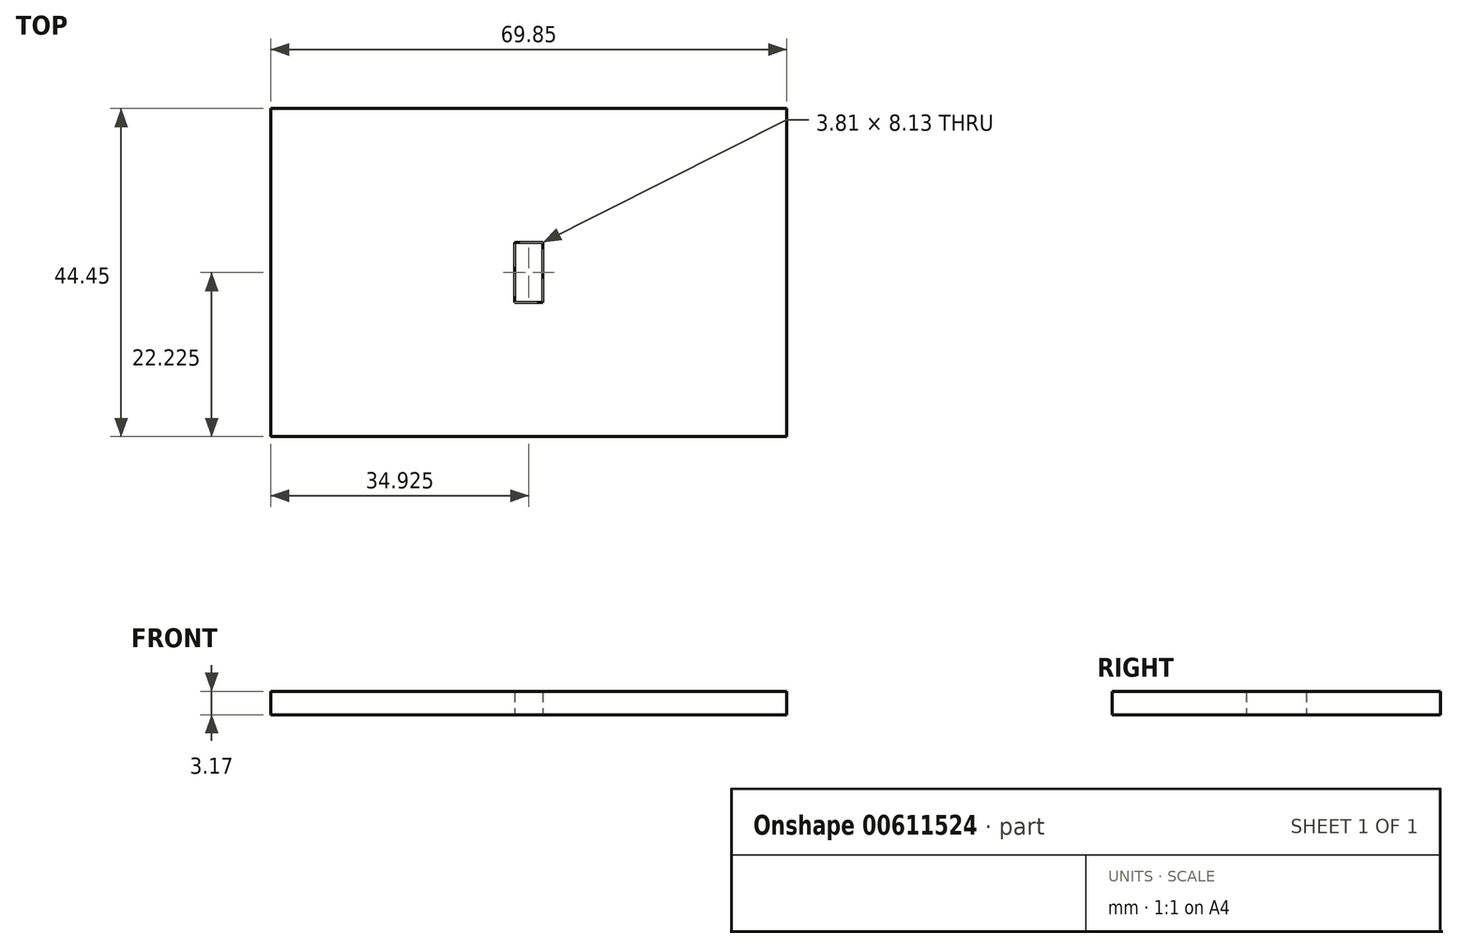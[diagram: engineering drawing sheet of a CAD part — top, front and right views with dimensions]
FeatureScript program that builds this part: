
annotation { "Feature Type Name" : "Feature", "Feature Type Description" : "" }
export const myFeature = defineFeature(function(context is Context, id is Id, definition is map)
    precondition{}
    {
        {
            var Q0;
            Q0=qCreatedBy(makeId("Top.planeOp"),FACE);
            var sketch = newSketch(context, id + "F0", { "sketchPlane" : qUnion([Q0])});
            skLineSegment(sketch, "E0.bottom", {"start": v(0, 0) * mm, "end": v(69.85, 0) * mm});
            skLineSegment(sketch, "E0.top", {"start": v(0, -44.45) * mm, "end": v(69.85, -44.45) * mm});
            skLineSegment(sketch, "E0.left", {"start": v(0, 0) * mm, "end": v(0, -44.45) * mm});
            skLineSegment(sketch, "E0.right", {"start": v(69.85, 0) * mm, "end": v(69.85, -44.45) * mm});
            skSolve(sketch);
        }
        {
            var Q0;
            Q0=makeQuery(id+"F0.imprint","IMPRINT",FACE,{"disambiguationData":[TD([[makeQuery(id+"F0.imprint","IMPRINT",EDGE,{"derivedFrom":sQuery(id+"F0.wireOp",EDGE,"E0.bottom")}),-1.0]])]});
            extrude(context, id + "F1", {"entities" : qUnion([Q0]), "depth" : 3.17 * mm, "offsetDistance" : 25.4 * mm});
        }
        {
            var Q0;
            Q0=makeQuery(id+"F1.opExtrude","CAP_FACE",FACE,{"disambiguationData":[OSD([sQuery(id+"F0.wireOp",EDGE,"E0.bottom"),sQuery(id+"F0.wireOp",EDGE,"E0.top"),sQuery(id+"F0.wireOp",EDGE,"E0.left"),sQuery(id+"F0.wireOp",EDGE,"E0.right")])],"isStart":true});
            var sketch = newSketch(context, id + "F2", { "sketchPlane" : qUnion([Q0])});
            skLineSegment(sketch, "E1", {"start": v(34.93, 44.45) * mm, "end": v(34.93, 0) * mm});
            skLineSegment(sketch, "E2", {"start": v(0, 22.23) * mm, "end": v(69.85, 22.23) * mm});
            skLineSegment(sketch, "E3", {"start": v(33.02, 22.23) * mm, "end": v(33.02, 18.16) * mm});
            skLineSegment(sketch, "E4", {"start": v(33.02, 18.16) * mm, "end": v(34.93, 18.16) * mm});
            skLineSegment(sketch, "E5.MirrorCS", {"start": v(36.83, 22.23) * mm, "end": v(36.83, 18.16) * mm});
            skLineSegment(sketch, "E6.MirrorCS", {"start": v(36.83, 18.16) * mm, "end": v(34.93, 18.16) * mm});
            skLineSegment(sketch, "E7.MirrorCS", {"start": v(36.83, 26.29) * mm, "end": v(34.93, 26.29) * mm});
            skLineSegment(sketch, "E8.MirrorCS", {"start": v(33.02, 26.29) * mm, "end": v(34.93, 26.29) * mm});
            skLineSegment(sketch, "E9.MirrorCS", {"start": v(33.02, 22.23) * mm, "end": v(33.02, 26.29) * mm});
            skLineSegment(sketch, "E10.MirrorCS", {"start": v(36.83, 22.23) * mm, "end": v(36.83, 26.29) * mm});
            skSolve(sketch);
        }
        {
            var Q0;
            {var subQ4=sQuery(id+"F2.wireOp",EDGE,"E5.MirrorCS");Q0=makeQuery(id+"F2.imprint","IMPRINT",FACE,{"disambiguationData":[TD([[makeQuery(id+"F2.imprint","IMPRINT",EDGE,{"derivedFrom":subQ4}),-1.0]])]});}
            var Q1;
            {var subQ4=sQuery(id+"F2.wireOp",EDGE,"E3");Q1=makeQuery(id+"F2.imprint","IMPRINT",FACE,{"disambiguationData":[TD([[makeQuery(id+"F2.imprint","IMPRINT",EDGE,{"derivedFrom":subQ4}),1.0]])]});}
            var Q2;
            {var subQ0=sQuery(id+"F2.wireOp",EDGE,"E7.MirrorCS");Q2=makeQuery(id+"F2.imprint","IMPRINT",FACE,{"disambiguationData":[TD([[makeQuery(id+"F2.imprint","IMPRINT",EDGE,{"derivedFrom":subQ0}),1.0]])]});}
            var Q3;
            {var subQ0=sQuery(id+"F2.wireOp",EDGE,"E8.MirrorCS");Q3=makeQuery(id+"F2.imprint","IMPRINT",FACE,{"disambiguationData":[TD([[makeQuery(id+"F2.imprint","IMPRINT",EDGE,{"derivedFrom":subQ0}),-1.0]])]});}
            extrude(context, id + "F3", {"entities" : qUnion([Q0, Q1, Q2, Q3]), "operationType" : NewBodyOperationType.REMOVE, "endBound" : BoundingType.UP_TO_NEXT, "oppositeDirection" : true, "depth" : 25.4 * mm, "offsetDistance" : 25.4 * mm});
        }
    });
